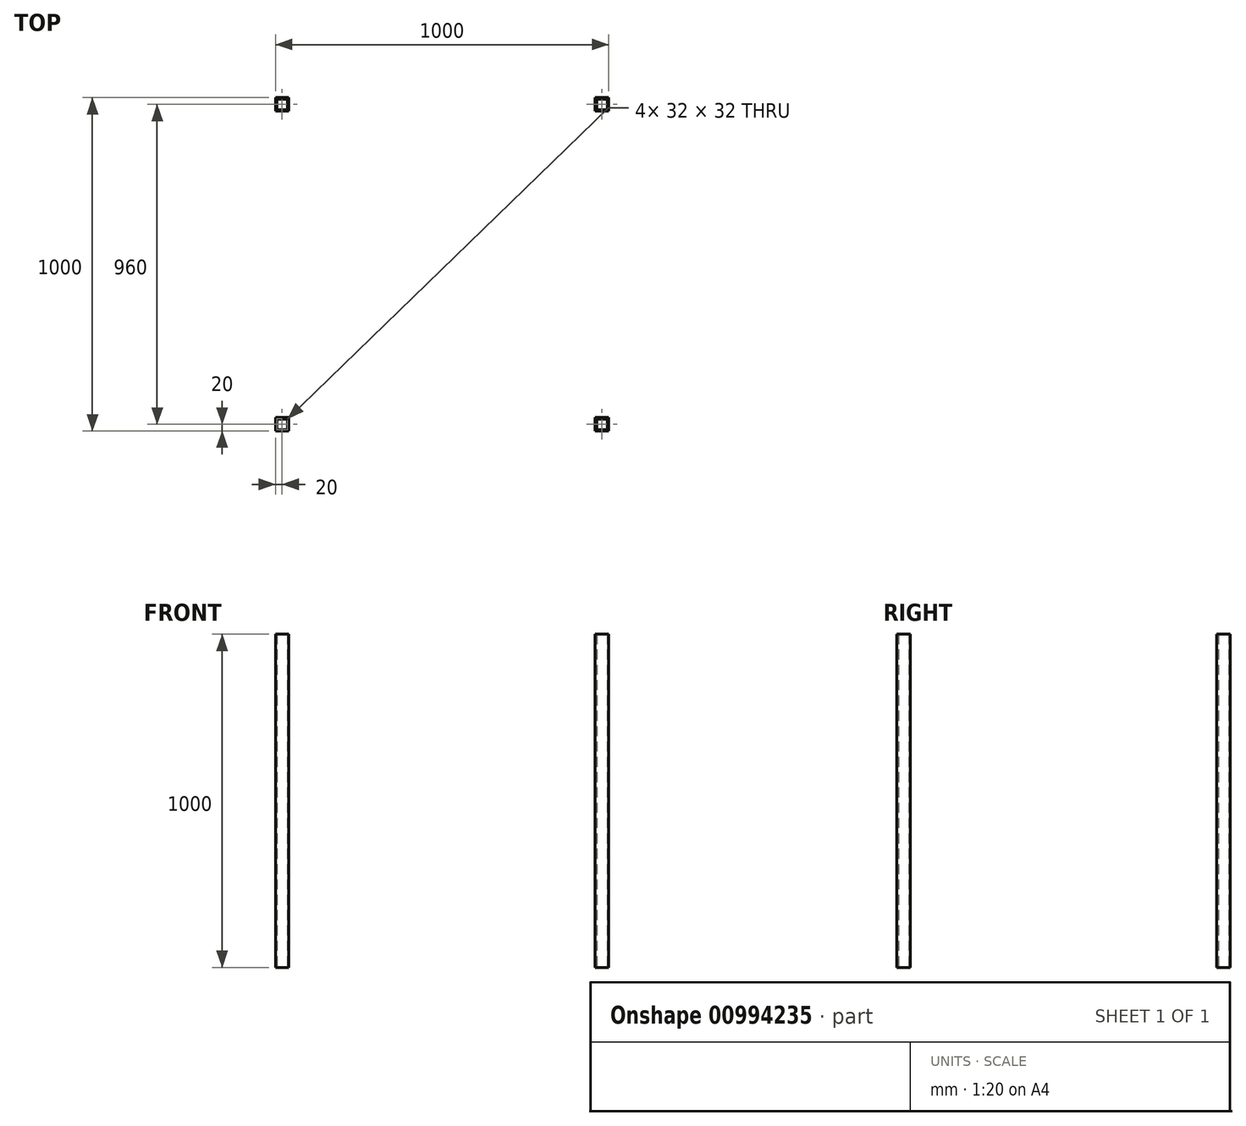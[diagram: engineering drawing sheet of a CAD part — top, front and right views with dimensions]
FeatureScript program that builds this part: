
annotation { "Feature Type Name" : "Feature", "Feature Type Description" : "" }
export const myFeature = defineFeature(function(context is Context, id is Id, definition is map)
    precondition{}
    {
        {
            var Q0;
            Q0=qCreatedBy(makeId("Top.planeOp"),FACE);
            var sketch = newSketch(context, id + "F0", { "sketchPlane" : qUnion([Q0])});
            skLineSegment(sketch, "E0.bottom", {"start": v(500, -500) * mm, "end": v(-500, -500) * mm, "construction": true});
            skLineSegment(sketch, "E0.top", {"start": v(500, 500) * mm, "end": v(-500, 500) * mm, "construction": true});
            skLineSegment(sketch, "E0.left", {"start": v(500, -500) * mm, "end": v(500, 500) * mm, "construction": true});
            skLineSegment(sketch, "E0.right", {"start": v(-500, -500) * mm, "end": v(-500, 500) * mm, "construction": true});
            skPoint(sketch, "E0.middle", {"position": v(0, 0) * mm});
            skLineSegment(sketch, "E1.bottom", {"start": v(-500, 460) * mm, "end": v(-460, 460) * mm});
            skLineSegment(sketch, "E1.top", {"start": v(-500, 500) * mm, "end": v(-460, 500) * mm});
            skLineSegment(sketch, "E1.left", {"start": v(-500, 460) * mm, "end": v(-500, 500) * mm});
            skLineSegment(sketch, "E1.right", {"start": v(-460, 460) * mm, "end": v(-460, 500) * mm});
            skPoint(sketch, "E1.middle", {"position": v(-480, 480) * mm});
            skLineSegment(sketch, "E2", {"start": v(0, 0) * mm, "end": v(0, 500) * mm, "construction": true});
            skLineSegment(sketch, "E3", {"start": v(0, 0) * mm, "end": v(-500, 0) * mm, "construction": true});
            skSolve(sketch);
        }
        {
            var Q0;
            Q0 = qSketchRegion(id + "F0", true);
            extrude(context, id + "F1", {"entities" : qUnion([Q0]), "depth" : 1000 * mm, "offsetDistance" : 25 * mm});
        }
        {
            var Q0;
            Q0=makeQuery(id+"F1.opExtrude","CAP_FACE",FACE,{"disambiguationData":[OSD([sQuery(id+"F0.wireOp",EDGE,"E1.bottom"),sQuery(id+"F0.wireOp",EDGE,"E1.top"),sQuery(id+"F0.wireOp",EDGE,"E1.left"),sQuery(id+"F0.wireOp",EDGE,"E1.right")])],"isStart":false});
            var Q1;
            Q1=makeQuery(id+"F1.opExtrude","CAP_FACE",FACE,{"disambiguationData":[OSD([sQuery(id+"F0.wireOp",EDGE,"E1.bottom"),sQuery(id+"F0.wireOp",EDGE,"E1.top"),sQuery(id+"F0.wireOp",EDGE,"E1.left"),sQuery(id+"F0.wireOp",EDGE,"E1.right")])],"isStart":true});
            shell(context, id + "F2", {"entities" : qUnion([Q0, Q1]), "thickness" : 4 * mm});
        }
        {
            var Q0;
            Q0=makeQuery(id+"F1.opExtrude","SWEPT_BODY",BODY,{"disambiguationData":[OSD([sQuery(id+"F0.wireOp",EDGE,"E1.bottom"),sQuery(id+"F0.wireOp",EDGE,"E1.top"),sQuery(id+"F0.wireOp",EDGE,"E1.left"),sQuery(id+"F0.wireOp",EDGE,"E1.right")])]});
            var Q1;
            Q1=qCreatedBy(makeId("Right.planeOp"),FACE);
            mirror(context, id + "F3", {"operationType" : NewBodyOperationType.ADD, "entities" : qUnion([Q0]), "mirrorPlane" : qUnion([Q1])});
        }
        {
            var Q0;
            Q0=makeQuery(id+"F1.opExtrude","SWEPT_BODY",BODY,{"disambiguationData":[OSD([sQuery(id+"F0.wireOp",EDGE,"E1.bottom"),sQuery(id+"F0.wireOp",EDGE,"E1.top"),sQuery(id+"F0.wireOp",EDGE,"E1.left"),sQuery(id+"F0.wireOp",EDGE,"E1.right")])]});
            var Q1;
            Q1=makeQuery(id+"F3.opPattern","COPY",BODY,{"derivedFrom":makeQuery(id+"F1.opExtrude","SWEPT_BODY",BODY,{"disambiguationData":[OSD([sQuery(id+"F0.wireOp",EDGE,"E1.bottom"),sQuery(id+"F0.wireOp",EDGE,"E1.top"),sQuery(id+"F0.wireOp",EDGE,"E1.left"),sQuery(id+"F0.wireOp",EDGE,"E1.right")])]}),"instanceName":"1"});
            var Q2;
            Q2=qCreatedBy(makeId("Front.planeOp"),FACE);
            mirror(context, id + "F4", {"operationType" : NewBodyOperationType.ADD, "entities" : qUnion([Q0, Q1]), "mirrorPlane" : qUnion([Q2])});
        }
    });
